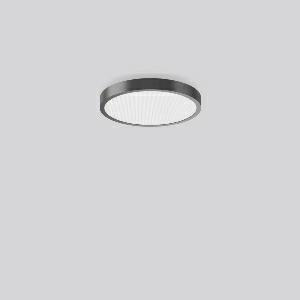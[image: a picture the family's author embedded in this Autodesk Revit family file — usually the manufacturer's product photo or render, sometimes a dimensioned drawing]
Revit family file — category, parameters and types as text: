
# Revit family: triona_round_a_312423_0031_2_76_e862
name_source: partatom
category: Lighting Fixtures
units: mm (PartAtom-declared; Revit-internal decimal feet)

## family parameters
Cut with Voids When Loaded = No
Host = Face
Light Source = No
Part Type = Normal
Room Calculation Point = No
Round Connector Dimension = Use Diameter
Shared = No

## types (1)
- TuneableWhite 846 (1 x LED Modul 846, 2700 lm, 4600)
    Apparent Load = 29 VA
    CIE Flux Codes = 58 87 97 100 100
    Color Rendering = 80
    Color Temperature = 4600
    Default Elevation = 1800 mm
    Description = Series: TRIONA round
Decorative round LED surface-mounted luminaire. Flat, seamless frame: aluminium extrusion profile, powder coated. Cover made of sheet steel, powder-coated. Light emission through a diffuser in plastic, opal/prismatic. Lightguide and diffuser made of non-yellowing plastic (PMMA). Lateral light emission (RZB SIDELITE technology) for above-average homogeneous light distribution. Tunable white versions, dynamically adjustable from 2700 K to 6500 K. Suitable for Ceiling mounting, Wall (surface). Tool-free mounting via bayonet connection. Electronic ballast included. Very easy installation thanks to Plug+Play connection. Perfect for office areas (RUG < 19) and environments with computer screens in accordance with EN 12464-1. Ideal for use as part of the Human Centric Lighting concept in connection with RZB light management systems. 
Colour: anthracite metallic (DB703)
Diameter: 461 mm
Height: 88 mm
Lamp: LED
Socket: without socket
Colour temperature: 2700K - 6500K
Colour rendering index (CRI): 80
System power: 29 W
Rated luminous flux: 2700 lm
Luminous efficiency: 93 lm/W
System power 2: 29 W
Rated luminous flux 2: 2550 lm
Luminous efficiency 2: 88 lm/W
System power 3: 30 W
Rated luminous flux 3: 2600 lm
Luminous efficiency 3: 87 lm/W
Control gear: Converter, dimmable, DALI
Protection class: I
Type of protection: IP 20
    Height = 88 mm
    Lamp = 1 x LED Modul 846
    Lamp Light Flux = 2700 lm
    Lamp count = 1
    Length = 461 mm
    Lifetime = 50000 h
    Luminous efficacy = 93 lm/W
    Manufacturer = RZB
    ModVariant = No
    Model = 312423.0031.2.76
    Mounting Place = Ceiling
    Mounting Type = Surface mounted
    Number of Poles = 1
    OnlyDefault = Yes
    Power Factor = 1
    Product Name = TRIONA round A
    Product group = Surface mounted modular luminaires
    ProductGroupID = 306
    Protection Class = Protection class I
    Protection Degree = IP 20
    RLX_Detail_Level = 1
    RLX_Emergency_Light_Flux = 0 lm
    RLX_Emergency_Type = 0
    RLX_Emergency_Type_DB = No
    RlxData = <blob elided: 30229 chars, md5=787f10da>
    Socket = socket
    Standby Power = 0 W
    System Light Flux = 2700 lm
    System Power = 29 W
    Type Comments = TuneableWhite 846
    Type Image = 312424.0031.jpg
    URL = http://relux.com
    VarID = tuneablewhite_846
    Voltage = 230 V
    Voltage Range = 220-240 V
    Weight = 0.00 kg
    Width = 0 mm  [stored 0 ft]

note: [stored X ft] marks values corroborated as IEEE doubles in the binary element streams (Revit-internal decimal feet)

## geometry (parser evidence)
native form markers: Blend x4, Sweep x11
no freeform markers — native parametric forms only
